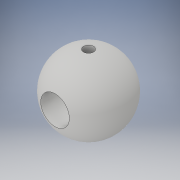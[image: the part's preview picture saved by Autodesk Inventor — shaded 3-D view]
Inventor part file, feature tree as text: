
AUTODESK INVENTOR PART (.ipt)
format: ipt  version: 2017 (Build 210142000, 142)  size: 146,944 bytes
history: native  units: in
note: dims shown in document units (in); Inventor stores cm internally (conversion verified against a paired STEP export)
features: sketch x3, plane x2, extrude x2, revolve x1
ambient origin geometry x8: Origin, YZ Plane, XZ Plane, XY Plane, X Axis, Y Axis, Z Axis, Center Point
bodies: Solid1 (feature_tree)
feature tree (8):
  revolve  "Revolution1"  Angle=90.0deg
  plane  "Work Plane1"
  plane  "Work Plane2"
  extrude  "Extrusion1"  Depth=0.104in
  extrude  "Extrusion2"  Depth=1.0in TaperAngle=0.0deg
  sketch  "Sketch1"  dims[d0=0.75in d1=90.0deg]
  sketch  "Sketch5"  dims[d11=0.375in d19=0.104in]
  sketch  "Sketch6"  dims[d20=0.375in d21=1.0in d22=0.0in d23=0.375in d24=0.295in d25=0.5in d26=0.0in]
